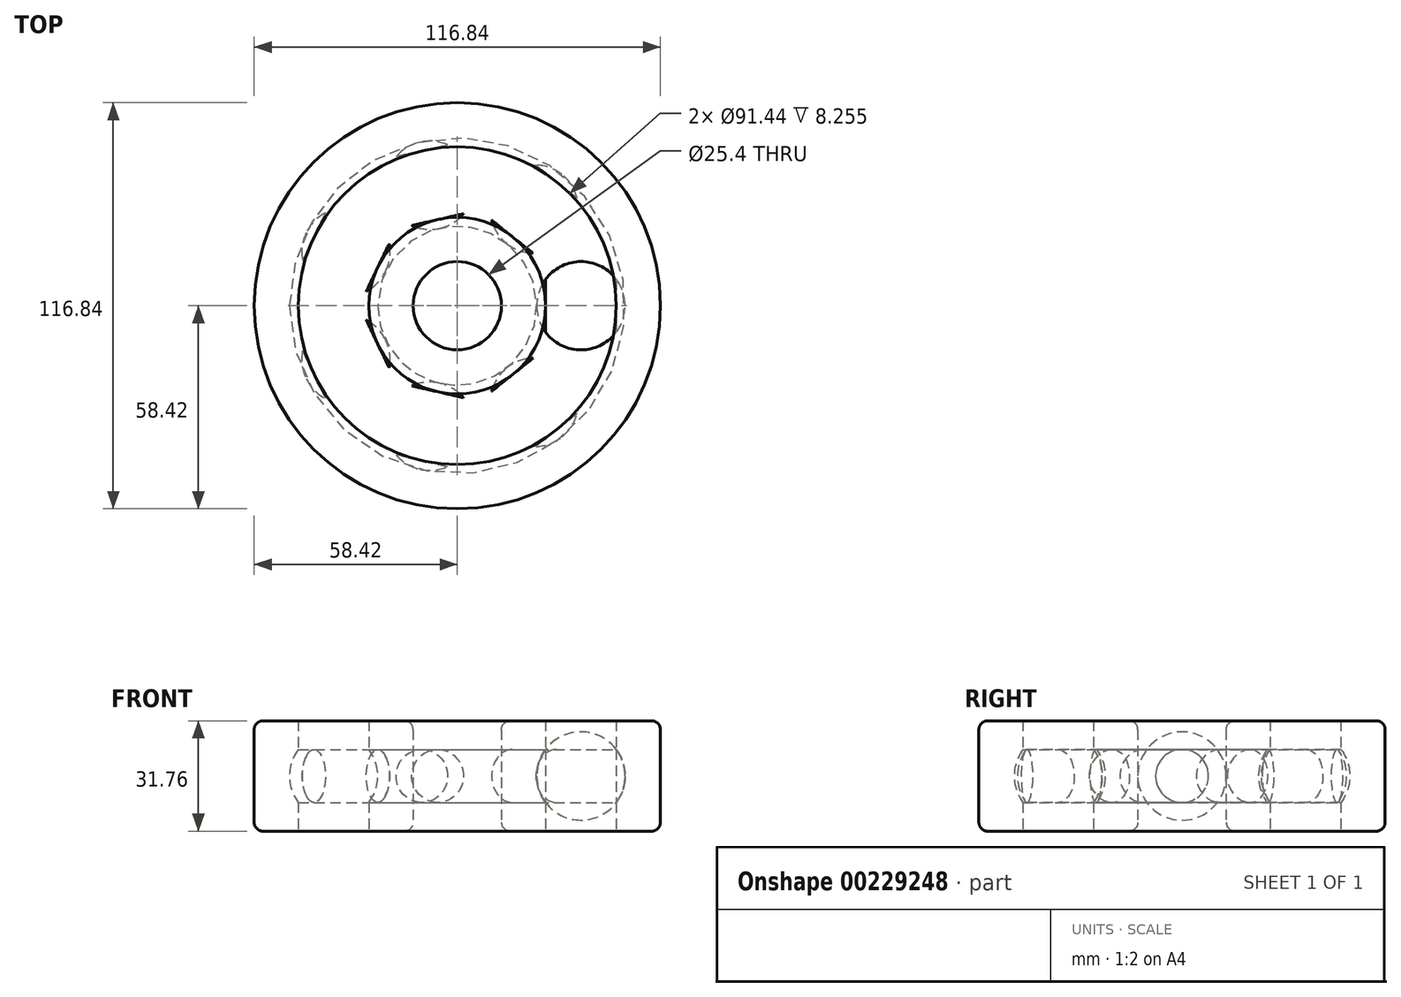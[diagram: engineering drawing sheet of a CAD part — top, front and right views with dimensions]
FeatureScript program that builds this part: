
annotation { "Feature Type Name" : "Feature", "Feature Type Description" : "" }
export const myFeature = defineFeature(function(context is Context, id is Id, definition is map)
    precondition{}
    {
        {
            var Q0;
            Q0=qCreatedBy(makeId("Front.planeOp"),FACE);
            var sketch = newSketch(context, id + "F0", { "sketchPlane" : qUnion([Q0])});
            skLineSegment(sketch, "E0", {"start": v(0, -15.88) * mm, "end": v(0, 15.88) * mm, "construction": true});
            skLineSegment(sketch, "E1", {"start": v(0, 0) * mm, "end": v(12.7, 0) * mm, "construction": true});
            skLineSegment(sketch, "E2", {"start": v(12.7, 0) * mm, "end": v(25.4, 0) * mm, "construction": true});
            skLineSegment(sketch, "E3", {"start": v(25.4, 0) * mm, "end": v(45.72, 0) * mm, "construction": true});
            skLineSegment(sketch, "E4", {"start": v(45.72, 0) * mm, "end": v(58.42, 0) * mm, "construction": true});
            skCircle(sketch, "E5", {"center": v(35.56, 0) * mm, "radius": 12.7 * mm});
            skLineSegment(sketch, "E6", {"start": v(12.7, -15.88) * mm, "end": v(12.7, 15.88) * mm});
            skLineSegment(sketch, "E7", {"start": v(25.4, -15.88) * mm, "end": v(25.4, 15.88) * mm});
            skLineSegment(sketch, "E8", {"start": v(45.72, -15.88) * mm, "end": v(45.72, 15.88) * mm});
            skLineSegment(sketch, "E9", {"start": v(58.42, -15.88) * mm, "end": v(58.42, 15.88) * mm});
            skLineSegment(sketch, "E10", {"start": v(12.7, 15.88) * mm, "end": v(25.4, 15.88) * mm});
            skLineSegment(sketch, "E11", {"start": v(12.7, -15.88) * mm, "end": v(25.4, -15.88) * mm});
            skLineSegment(sketch, "E12", {"start": v(45.72, -15.88) * mm, "end": v(58.42, -15.88) * mm});
            skLineSegment(sketch, "E13", {"start": v(58.42, 15.88) * mm, "end": v(45.72, 15.88) * mm});
            skLineSegment(sketch, "E14", {"start": v(22.86, 0) * mm, "end": v(48.26, 0) * mm});
            skSolve(sketch);
        }
        {
            var Q0;
            Q0=makeQuery(id+"F0.imprint","IMPRINT",FACE,{"disambiguationData":[TD([[makeQuery(id+"F0.imprint","IMPRINT",EDGE,{"derivedFrom":sQuery(id+"F0.wireOp",EDGE,"E6")}),-1.0]])]});
            var Q1;
            Q1=sQuery(id+"F0.wireOp",EDGE,"E0");
            revolve(context, id + "F1", {"entities" : qUnion([Q0]), "axis" : qUnion([Q1]), "revolveType" : RevolveType.FULL});
        }
        {
            var Q0;
            Q0=makeQuery(id+"F0.imprint","IMPRINT",FACE,{"disambiguationData":[TD([[makeQuery(id+"F0.imprint","IMPRINT",EDGE,{"derivedFrom":sQuery(id+"F0.wireOp",EDGE,"E9")}),1.0]])]});
            var Q1;
            Q1=sQuery(id+"F0.wireOp",EDGE,"E0");
            revolve(context, id + "F2", {"entities" : qUnion([Q0]), "axis" : qUnion([Q1]), "revolveType" : RevolveType.FULL});
        }
        {
            var Q0;
            {var subQ0=sQuery(id+"F0.wireOp",EDGE,"E14");var subQ1=sQuery(id+"F0.wireOp",EDGE,"E5");var subQ2=makeQuery(id+"F0.imprint","INTERSECT",VERTEX,{"disambiguationData":[OD(0.0)],"derivedFrom":[subQ1,subQ0]});Q0=makeQuery(id+"F0.imprint","IMPRINT",FACE,{"disambiguationData":[TD([[makeQuery(id+"F0.imprint","IMPRINT",EDGE,{"disambiguationData":[TD([[subQ2,1.0]])],"derivedFrom":subQ1}),1.0]])]});}
            var Q1;
            {var subQ0=sQuery(id+"F0.wireOp",EDGE,"E8");var subQ1=sQuery(id+"F0.wireOp",EDGE,"E5");var subQ2=makeQuery(id+"F0.imprint","INTERSECT",VERTEX,{"disambiguationData":[OD(0.0)],"derivedFrom":[subQ1,subQ0]});Q1=makeQuery(id+"F0.imprint","IMPRINT",FACE,{"disambiguationData":[TD([[makeQuery(id+"F0.imprint","IMPRINT",EDGE,{"disambiguationData":[TD([[subQ2,-1.0]])],"derivedFrom":subQ1}),1.0]])]});}
            var Q2;
            {var subQ0=sQuery(id+"F0.wireOp",EDGE,"E14");var subQ1=sQuery(id+"F0.wireOp",EDGE,"E5");var subQ2=makeQuery(id+"F0.imprint","INTERSECT",VERTEX,{"disambiguationData":[OD(1.0)],"derivedFrom":[subQ1,subQ0]});Q2=makeQuery(id+"F0.imprint","IMPRINT",FACE,{"disambiguationData":[TD([[makeQuery(id+"F0.imprint","IMPRINT",EDGE,{"disambiguationData":[TD([[subQ2,-1.0]])],"derivedFrom":subQ1}),1.0]])]});}
            var Q3;
            Q3=sQuery(id+"F0.wireOp",EDGE,"E14");
            revolve(context, id + "F3", {"entities" : qUnion([Q0, Q1, Q2]), "axis" : qUnion([Q3]), "revolveType" : RevolveType.FULL});
        }
        {
            var Q0;
            Q0=makeQuery(id+"F3.opRevolve","SWEPT_BODY",BODY,{"disambiguationData":[OSD([sQuery(id+"F0.wireOp",EDGE,"E5"),sQuery(id+"F0.wireOp",EDGE,"E14")])]});
            var Q1;
            Q1=sQuery(id+"F0.wireOp",EDGE,"E0");
            circularPattern(context, id + "F4", {"entities" : qUnion([Q0]), "axis" : qUnion([Q1]), "angle" : 360 * degree, "instanceCount" : 7, "equalSpace" : true});
        }
        {
            var Q0;
            Q0=makeQuery(id+"F2.opRevolve","SWEPT_EDGE",EDGE,{"disambiguationData":[OSD([sQuery(id+"F0.wireOp",EDGE,"E9"),sQuery(id+"F0.wireOp",EDGE,"E13")])]});
            var Q1;
            Q1=makeQuery(id+"F2.opRevolve","SWEPT_EDGE",EDGE,{"disambiguationData":[OSD([sQuery(id+"F0.wireOp",EDGE,"E9"),sQuery(id+"F0.wireOp",EDGE,"E12")])]});
            var Q2;
            Q2=makeQuery(id+"F1.opRevolve","SWEPT_EDGE",EDGE,{"disambiguationData":[OSD([sQuery(id+"F0.wireOp",EDGE,"E6"),sQuery(id+"F0.wireOp",EDGE,"E10")])]});
            var Q3;
            Q3=makeQuery(id+"F1.opRevolve","SWEPT_EDGE",EDGE,{"disambiguationData":[OSD([sQuery(id+"F0.wireOp",EDGE,"E6"),sQuery(id+"F0.wireOp",EDGE,"E11")])]});
            fillet(context, id + "F5", {"entities" : qUnion([Q0, Q1, Q2, Q3]), "radius" : 2.54 * mm, "tangentPropagation" : true, "allowEdgeOverflow" : false});
        }
    });
